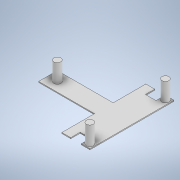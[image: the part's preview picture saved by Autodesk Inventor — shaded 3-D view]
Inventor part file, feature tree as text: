
AUTODESK INVENTOR PART (.ipt)
format: ipt  version: 2020 (Build 240168000, 168)  size: 136,704 bytes
history: native  units: mm
features: extrude x2, sketch x2
ambient origin geometry x8: Origin, YZ Plane, XZ Plane, XY Plane, X Axis, Y Axis, Z Axis, Center Point
bodies: Solid1 (feature_tree)
feature tree (4):
  extrude  "Extrusion1"  Depth=180.0mm
  extrude  "Extrusion2"  Depth=20.0mm
  sketch  "Sketch1"  dims[d0=180.0mm d1=180.0mm]
  sketch  "Sketch2"  dims[d3=20.0mm d4=20.0mm d5=20.0mm d6=20.0mm d7=40.0mm d8=70.0mm d9=70.0mm d10=90.0mm d11=2.0mm d12=0.0mm d13=15.0mm d14=15.0mm d15=15.0mm d16=9.0mm d17=9.3045mm d18=9.0mm d19=9.3045mm d20=20.0mm d21=40.0mm d22=0.0mm]
